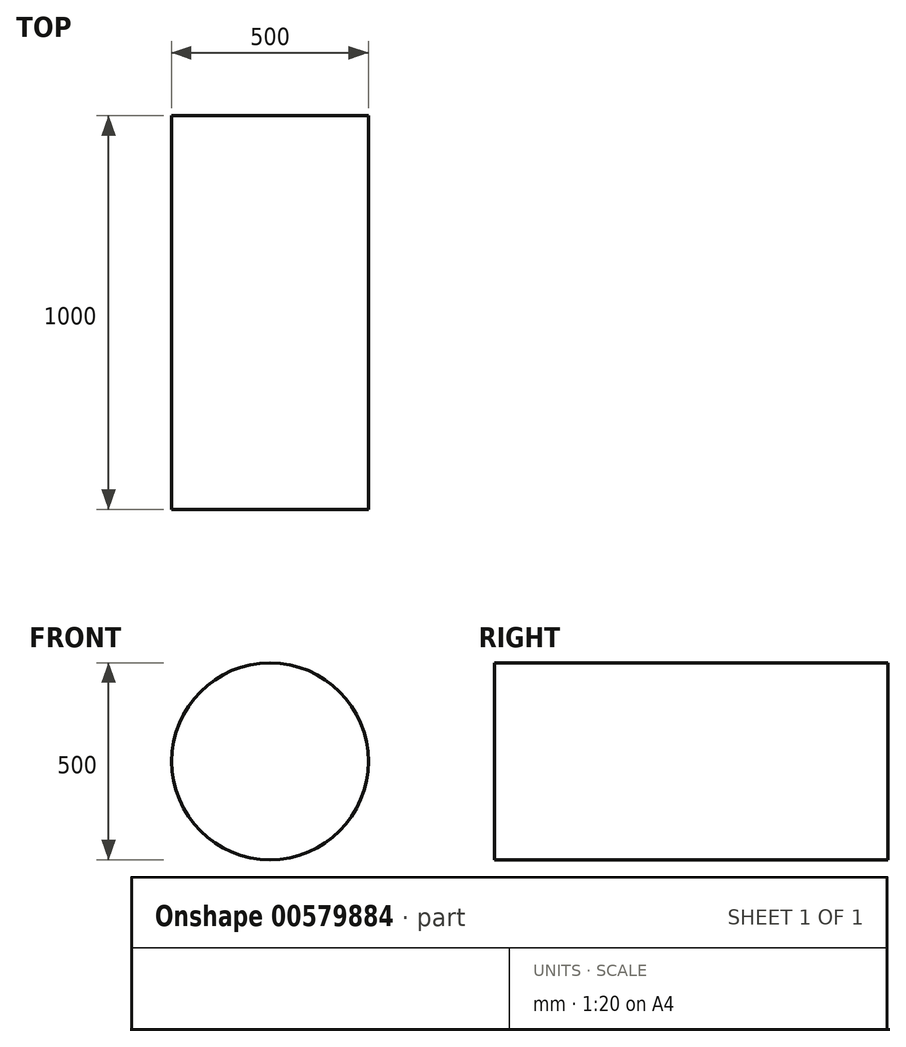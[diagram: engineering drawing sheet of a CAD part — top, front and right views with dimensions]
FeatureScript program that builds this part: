
annotation { "Feature Type Name" : "Feature", "Feature Type Description" : "" }
export const myFeature = defineFeature(function(context is Context, id is Id, definition is map)
    precondition{}
    {
        {
            var Q0;
            Q0=qCreatedBy(makeId("Front.planeOp"),FACE);
            var sketch = newSketch(context, id + "F0", { "sketchPlane" : qUnion([Q0])});
            skCircle(sketch, "E0", {"center": v(0, 0) * mm, "radius": 250 * mm});
            skSolve(sketch);
        }
        {
            var Q0;
            Q0 = qSketchRegion(id + "F0", true);
            extrude(context, id + "F1", {"entities" : qUnion([Q0]), "oppositeDirection" : true, "depth" : 1000 * mm, "offsetDistance" : 25 * mm});
        }
    });
